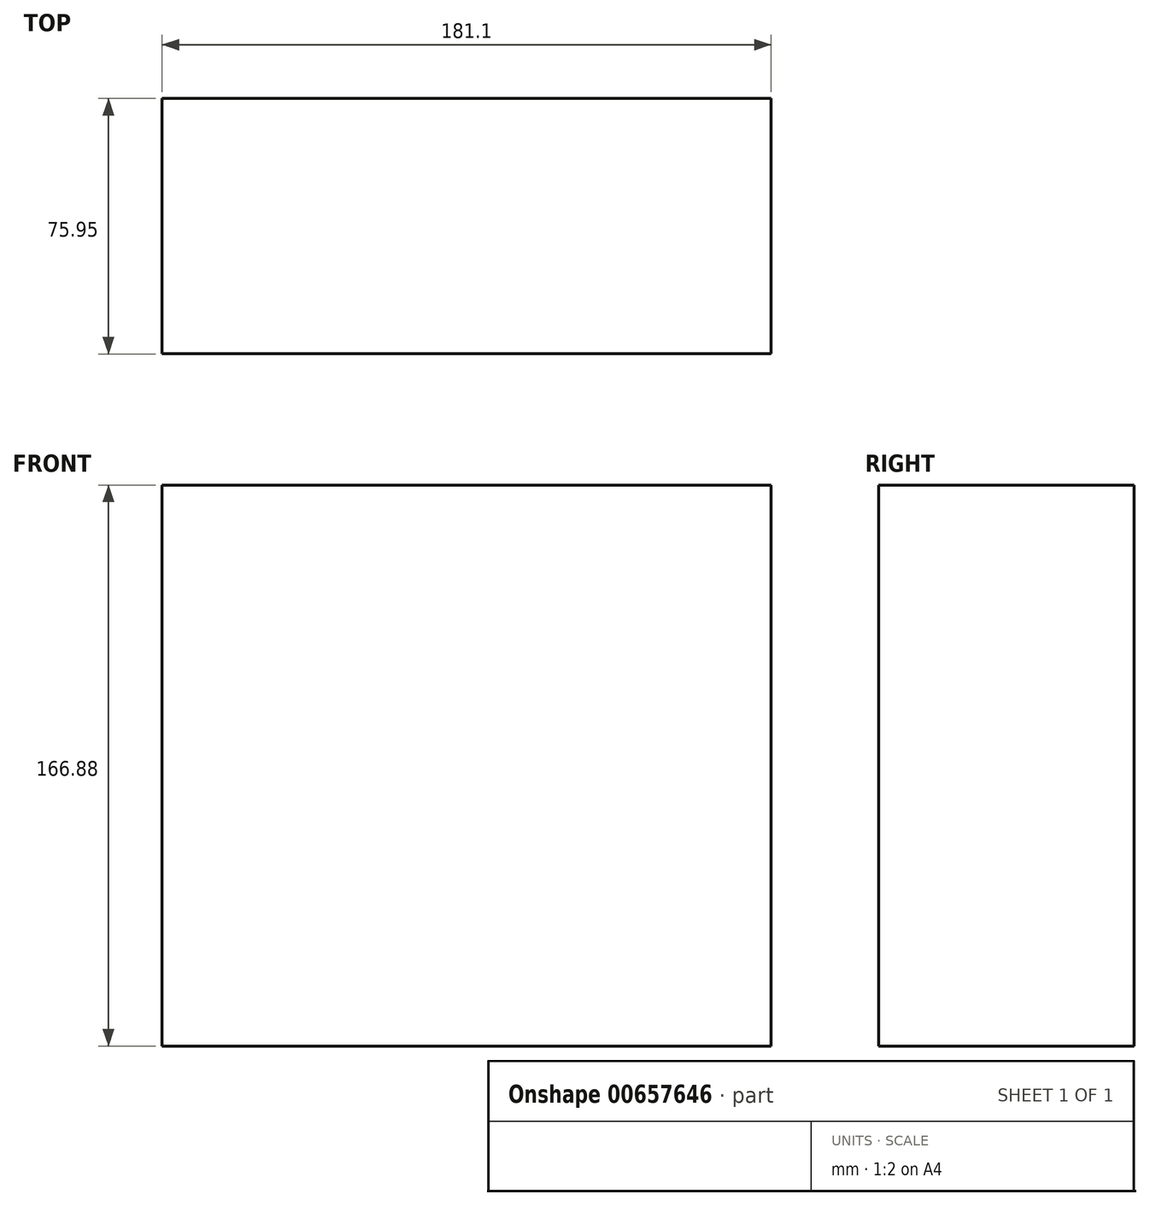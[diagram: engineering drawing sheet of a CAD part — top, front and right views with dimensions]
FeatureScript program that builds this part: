
annotation { "Feature Type Name" : "Feature", "Feature Type Description" : "" }
export const myFeature = defineFeature(function(context is Context, id is Id, definition is map)
    precondition{}
    {
        {
            var Q0;
            Q0=qCreatedBy(makeId("Top.planeOp"),FACE);
            var sketch = newSketch(context, id + "F0", { "sketchPlane" : qUnion([Q0])});
            skLineSegment(sketch, "E0.bottom", {"start": v(0, 0) * mm, "end": v(181.1, 0) * mm});
            skLineSegment(sketch, "E0.top", {"start": v(0, -75.95) * mm, "end": v(181.1, -75.95) * mm});
            skLineSegment(sketch, "E0.left", {"start": v(0, 0) * mm, "end": v(0, -75.95) * mm});
            skLineSegment(sketch, "E0.right", {"start": v(181.1, 0) * mm, "end": v(181.1, -75.95) * mm});
            skSolve(sketch);
        }
        {
            var Q0;
            Q0=makeQuery(id+"F0.imprint","IMPRINT",FACE,{"disambiguationData":[TD([[makeQuery(id+"F0.imprint","IMPRINT",EDGE,{"derivedFrom":sQuery(id+"F0.wireOp",EDGE,"E0.bottom")}),-1.0]])]});
            extrude(context, id + "F1", {"entities" : qUnion([Q0]), "depth" : 166.88 * mm, "offsetDistance" : 25.4 * mm});
        }
    });
